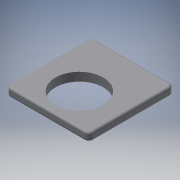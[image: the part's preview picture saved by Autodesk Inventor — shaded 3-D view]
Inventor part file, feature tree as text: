
AUTODESK INVENTOR PART (.ipt)
format: ipt  version: 2018 (Build 220112000, 112)  size: 143,360 bytes
history: native  units: mm
features: extrude x2, fillet x2, sketch x1, projected_geometry x1
ambient origin geometry x8: Origin, YZ Plane, XZ Plane, XY Plane, X Axis, Y Axis, Z Axis, Center Point
bodies: Solid1 (feature_tree)
feature tree (6):
  extrude  "Extrusion1"  Depth=2.0mm TaperAngle=0.0deg
  extrude  "Extrusion2"  Depth=0.5mm
  fillet  "Fillet3"  Radius=7.5mm
  fillet  "Fillet4"  Radius=5.0mm
  sketch  "Sketch2"  dims[d0=11.2mm d1=2.0mm d2=0.0mm d5=7.5mm d6=7.5mm d7=5.0mm d8=0.0mm d9=0.5mm d10=0.5mm]
  projected_geometry  "Projected Loop1"
